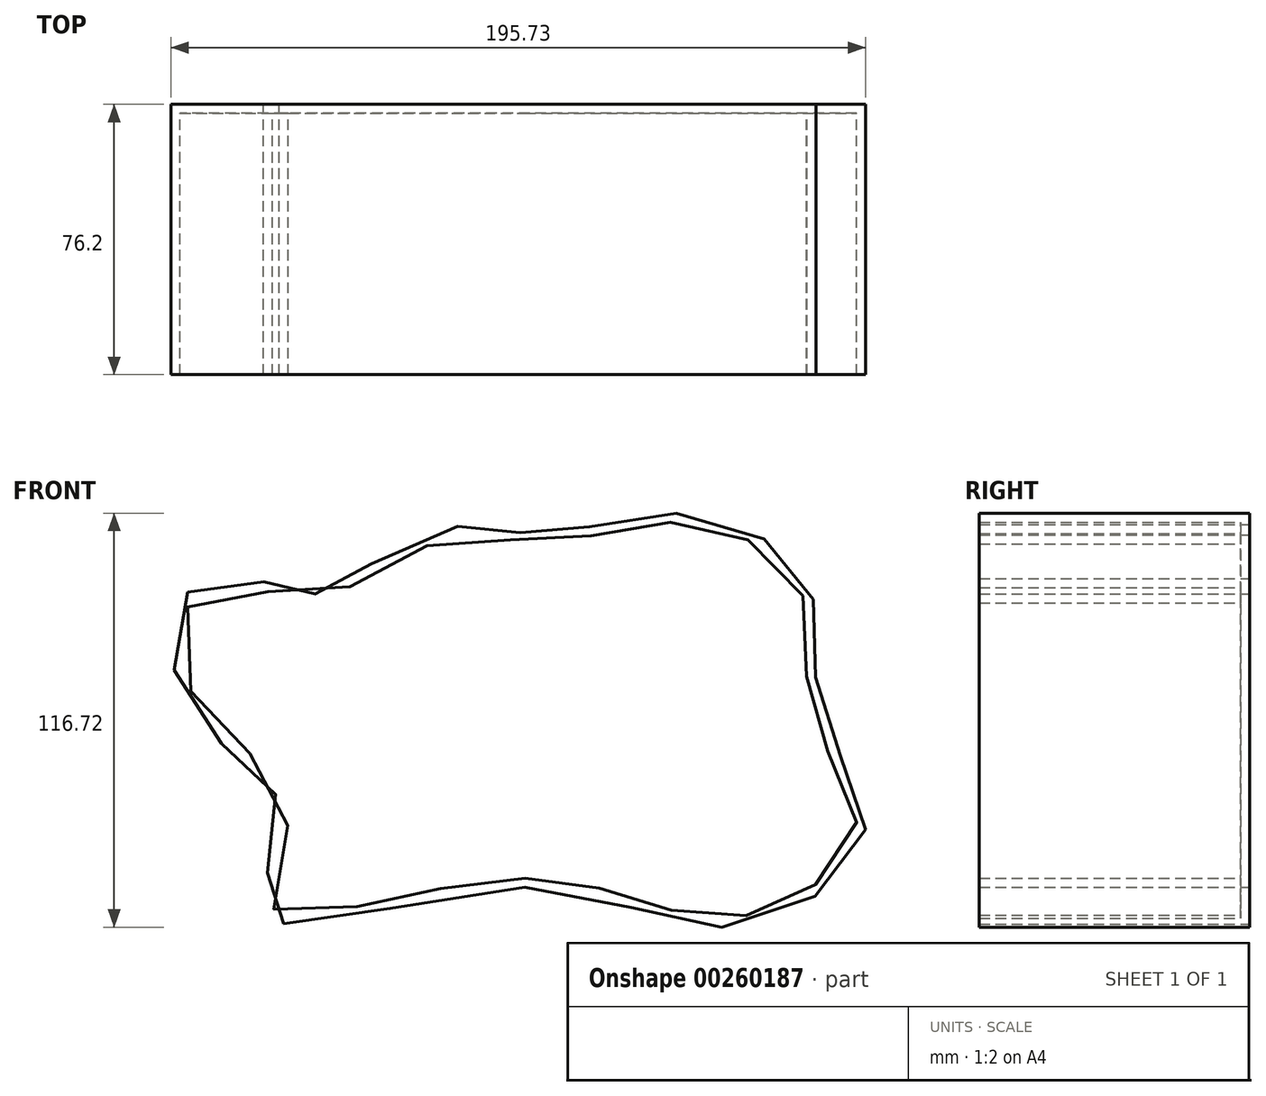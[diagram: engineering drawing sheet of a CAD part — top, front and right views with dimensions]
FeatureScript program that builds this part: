
annotation { "Feature Type Name" : "Feature", "Feature Type Description" : "" }
export const myFeature = defineFeature(function(context is Context, id is Id, definition is map)
    precondition{}
    {
        {
            var Q0;
            Q0=qCreatedBy(makeId("Front.planeOp"),FACE);
            var sketch = newSketch(context, id + "F0", { "sketchPlane" : qUnion([Q0])});
            skPoint(sketch, "E0.visualSharp", {"position": v(-50.36, 19.21) * mm});
            skPoint(sketch, "E1.visualSharp", {"position": v(-50.36, -82.39) * mm});
            skPoint(sketch, "E2.visualSharp", {"position": v(102.04, -82.39) * mm});
            skPoint(sketch, "E3.visualSharp", {"position": v(102.04, 19.21) * mm});
            skFitSpline(sketch, "E4", {"points": [v(9.1, 26.66) * mm, v(-29.04, 8.2) * mm, v(-34.26, 8.2) * mm, v(-65.64, 9.12) * mm, v(-65.02, -26.86) * mm, v(-41.34, -51.47) * mm, v(-44.41, -83.14) * mm, v(28.17, -75.15) * mm, v(86, -86.22) * mm, v(123.82, -60.08) * mm, v(111.21, -25.01) * mm, v(107.83, 10.35) * mm, v(71.54, 30.35) * mm, v(32.17, 24.2) * mm, v(9.1, 26.66) * mm]});
            skSolve(sketch);
        }
        {
            var Q0;
            Q0 = qSketchRegion(id + "F0", true);
            extrude(context, id + "F1", {"entities" : qUnion([Q0]), "depth" : 76.2 * mm});
        }
        {
            var Q0;
            Q0=makeQuery(id+"F1.opExtrude","CAP_FACE",FACE,{"disambiguationData":[OSD([sQuery(id+"F0.wireOp",EDGE,"E4")])],"isStart":false});
            shell(context, id + "F2", {"entities" : qUnion([Q0]), "thickness" : 2.54 * mm});
        }
    });
